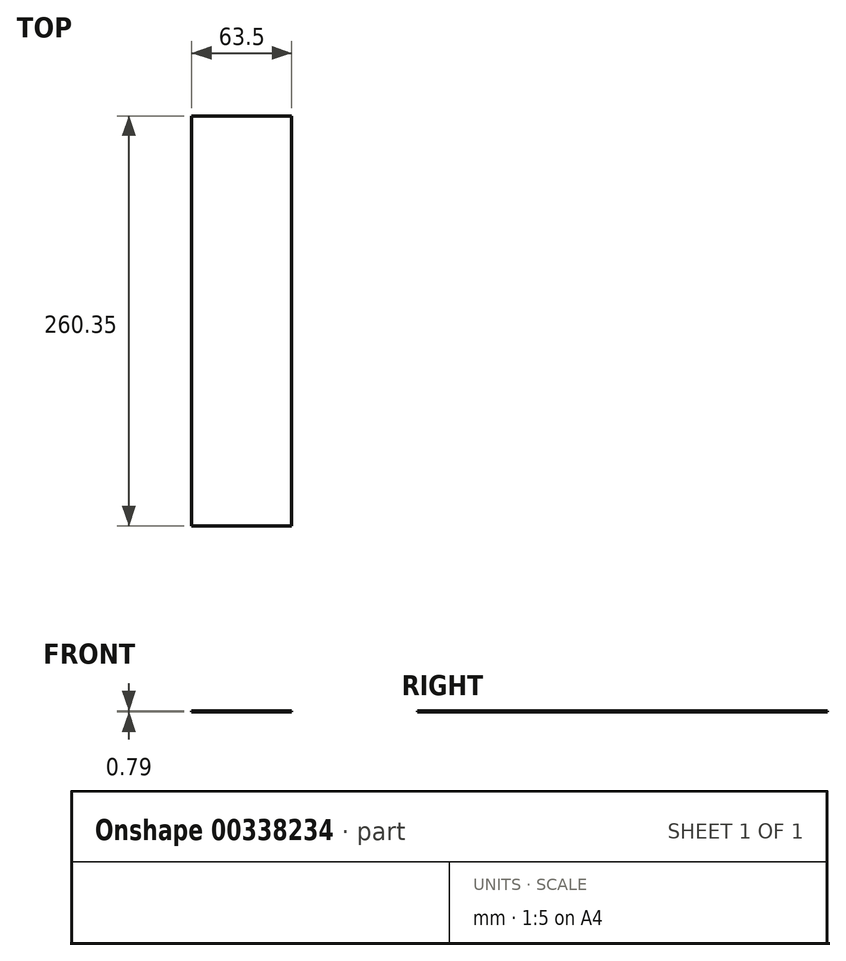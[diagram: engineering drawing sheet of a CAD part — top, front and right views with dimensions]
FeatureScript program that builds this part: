
annotation { "Feature Type Name" : "Feature", "Feature Type Description" : "" }
export const myFeature = defineFeature(function(context is Context, id is Id, definition is map)
    precondition{}
    {
        {
            var Q0;
            Q0=qCreatedBy(makeId("Top.planeOp"),FACE);
            var sketch = newSketch(context, id + "F0", { "sketchPlane" : qUnion([Q0])});
            skLineSegment(sketch, "E0.bottom", {"start": v(0, 0) * mm, "end": v(63.5, 0) * mm});
            skLineSegment(sketch, "E0.top", {"start": v(0, -260.35) * mm, "end": v(63.5, -260.35) * mm});
            skLineSegment(sketch, "E0.left", {"start": v(0, 0) * mm, "end": v(0, -260.35) * mm});
            skLineSegment(sketch, "E0.right", {"start": v(63.5, 0) * mm, "end": v(63.5, -260.35) * mm});
            skSolve(sketch);
        }
        {
            var Q0;
            Q0 = qSketchRegion(id + "F0", true);
            extrude(context, id + "F1", {"entities" : qUnion([Q0]), "depth" : 0.8 * mm});
        }
    });
